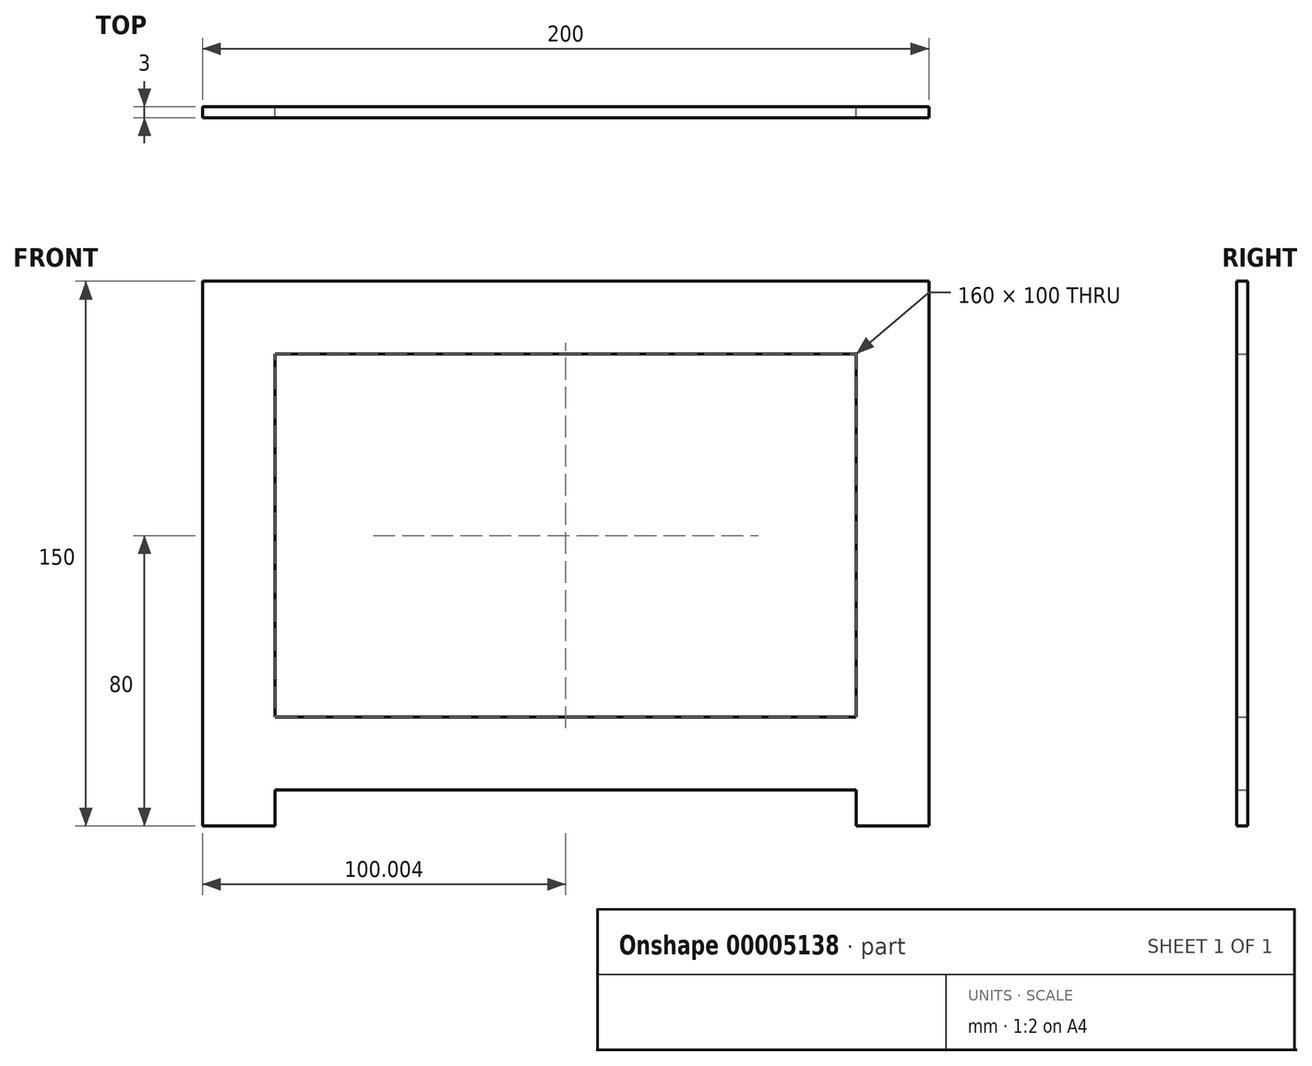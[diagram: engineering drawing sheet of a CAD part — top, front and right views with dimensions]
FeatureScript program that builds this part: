
annotation { "Feature Type Name" : "Feature", "Feature Type Description" : "" }
export const myFeature = defineFeature(function(context is Context, id is Id, definition is map)
    precondition{}
    {
        {
            var Q0;
            Q0=qCreatedBy(makeId("Front.planeOp"),FACE);
            var sketch = newSketch(context, id + "F0", { "sketchPlane" : qUnion([Q0])});
            skLineSegment(sketch, "E0.bottom", {"start": v(-100.24, 71.97) * mm, "end": v(99.76, 71.97) * mm});
            skLineSegment(sketch, "E0.top", {"start": v(-100.24, -78.03) * mm, "end": v(99.76, -78.03) * mm});
            skLineSegment(sketch, "E0.left", {"start": v(-100.24, 71.97) * mm, "end": v(-100.24, -78.03) * mm});
            skLineSegment(sketch, "E0.right", {"start": v(99.76, 71.97) * mm, "end": v(99.76, -78.03) * mm});
            skSolve(sketch);
        }
        {
            var Q0;
            Q0=makeQuery(id+"F0.imprint","IMPRINT",FACE,{"disambiguationData":[TD([[makeQuery(id+"F0.imprint","IMPRINT",EDGE,{"derivedFrom":sQuery(id+"F0.wireOp",EDGE,"E0.bottom")}),-1.0]])]});
            var sketch = newSketch(context, id + "F1", { "sketchPlane" : qUnion([Q0])});
            skLineSegment(sketch, "E1.bottom", {"start": v(-80.24, 51.97) * mm, "end": v(79.76, 51.97) * mm});
            skLineSegment(sketch, "E1.top", {"start": v(-80.24, -48.03) * mm, "end": v(79.76, -48.03) * mm});
            skLineSegment(sketch, "E1.left", {"start": v(-80.24, 51.97) * mm, "end": v(-80.24, -48.03) * mm});
            skLineSegment(sketch, "E1.right", {"start": v(79.76, 51.97) * mm, "end": v(79.76, -48.03) * mm});
            skSolve(sketch);
        }
        {
            var Q0;
            Q0=makeQuery(id+"F0.imprint","IMPRINT",FACE,{"disambiguationData":[TD([[makeQuery(id+"F0.imprint","IMPRINT",EDGE,{"derivedFrom":sQuery(id+"F0.wireOp",EDGE,"E0.bottom")}),-1.0]])]});
            var sketch = newSketch(context, id + "F2", { "sketchPlane" : qUnion([Q0])});
            skLineSegment(sketch, "E2", {"start": v(-80.24, -78.03) * mm, "end": v(-80.24, -68.03) * mm});
            skLineSegment(sketch, "E3", {"start": v(-80.24, -68.03) * mm, "end": v(79.76, -68.03) * mm});
            skLineSegment(sketch, "E4", {"start": v(79.76, -68.03) * mm, "end": v(79.76, -78.03) * mm});
            skSolve(sketch);
        }
        {
            var Q0;
            {var subQ3=sQuery(id+"F2.wireOp",EDGE,"E2");Q0=makeQuery(id+"F2.imprint","IMPRINT",FACE,{"disambiguationData":[TD([[makeQuery(id+"F2.imprint","IMPRINT",EDGE,{"derivedFrom":subQ3}),1.0]])]});}
            extrude(context, id + "F3", {"entities" : qUnion([Q0]), "depth" : 3 * mm});
        }
        {
            var Q0;
            Q0=makeQuery(id+"F1.imprint","IMPRINT",FACE,{"disambiguationData":[TD([[makeQuery(id+"F1.imprint","IMPRINT",EDGE,{"derivedFrom":sQuery(id+"F1.wireOp",EDGE,"E1.bottom")}),-1.0]])]});
            extrude(context, id + "F4", {"entities" : qUnion([Q0]), "operationType" : NewBodyOperationType.REMOVE, "endBound" : BoundingType.THROUGH_ALL, "depth" : 25 * mm});
        }
    });
